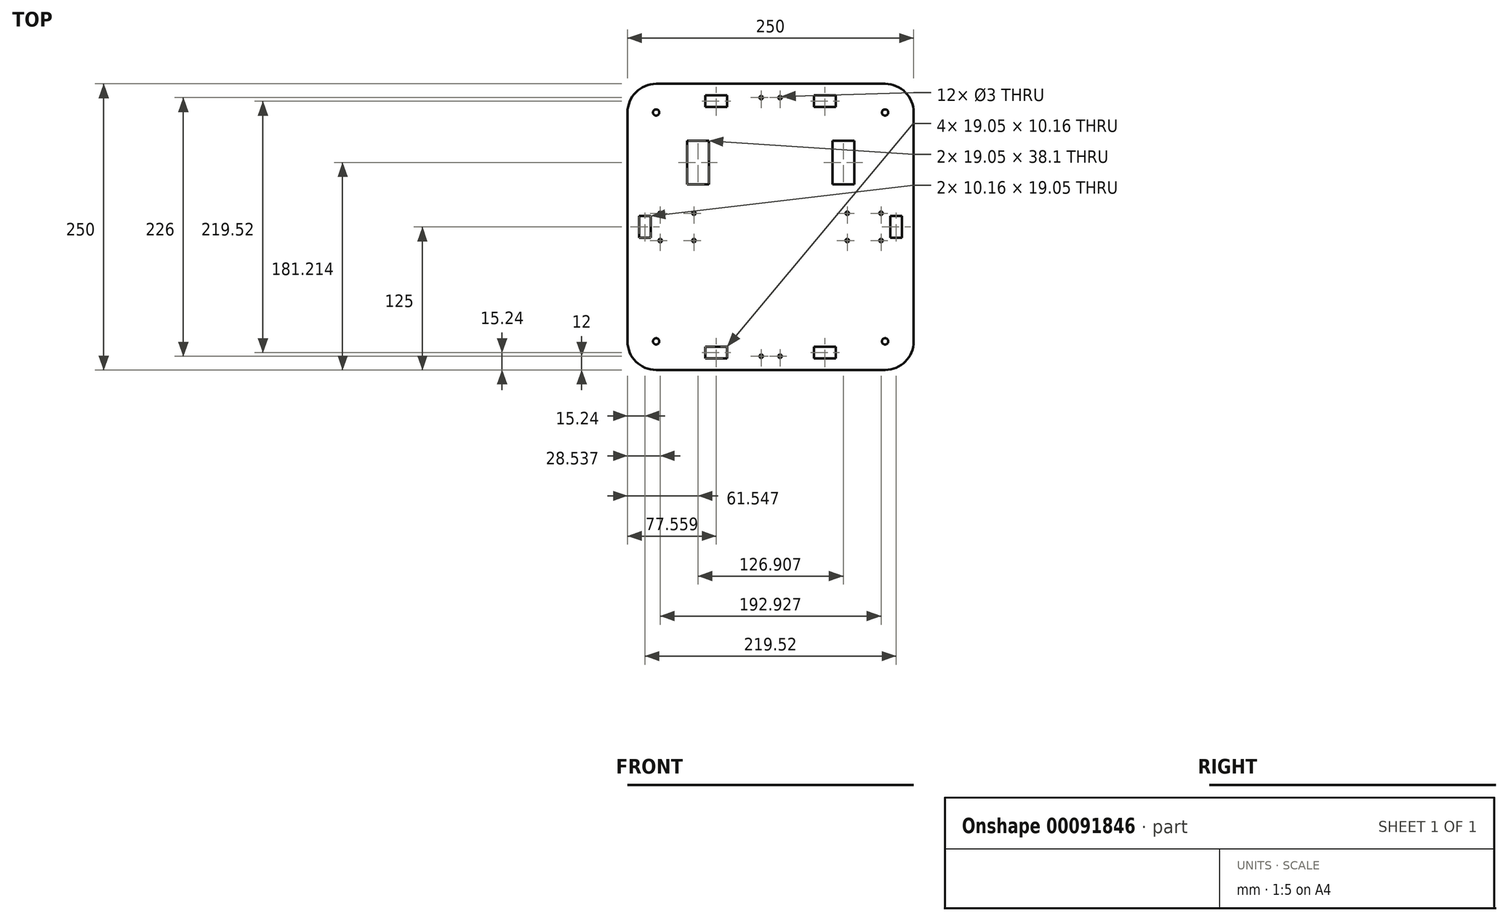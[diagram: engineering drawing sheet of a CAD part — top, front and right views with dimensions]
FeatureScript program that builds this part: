
annotation { "Feature Type Name" : "Feature", "Feature Type Description" : "" }
export const myFeature = defineFeature(function(context is Context, id is Id, definition is map)
    precondition{}
    {
        {
            var Q0;
            Q0=qCreatedBy(makeId("Top.planeOp"),FACE);
            var sketch = newSketch(context, id + "F0", { "sketchPlane" : qUnion([Q0])});
            skLineSegment(sketch, "E0.bottom", {"start": v(-100, 125) * mm, "end": v(100, 125) * mm});
            skLineSegment(sketch, "E0.top", {"start": v(-100, -125) * mm, "end": v(100, -125) * mm});
            skLineSegment(sketch, "E0.left", {"start": v(-125, 100) * mm, "end": v(-125, -100) * mm});
            skLineSegment(sketch, "E0.right", {"start": v(125, 100) * mm, "end": v(125, -100) * mm});
            skPoint(sketch, "E1.visualSharp", {"position": v(-125, -125) * mm});
            skArc(sketch, "E1.filletArc", {"start": v(-125, -100) * mm, "mid": v(-117.68, -117.68) * mm, "end": v(-100, -125) * mm});
            skPoint(sketch, "E2.visualSharp", {"position": v(-125, 125) * mm});
            skArc(sketch, "E2.filletArc", {"start": v(-100, 125) * mm, "mid": v(-117.68, 117.68) * mm, "end": v(-125, 100) * mm});
            skPoint(sketch, "E3.visualSharp", {"position": v(125, -125) * mm});
            skArc(sketch, "E3.filletArc", {"start": v(100, -125) * mm, "mid": v(117.68, -117.68) * mm, "end": v(125, -100) * mm});
            skPoint(sketch, "E4.visualSharp", {"position": v(125, 125) * mm});
            skArc(sketch, "E4.filletArc", {"start": v(125, 100) * mm, "mid": v(117.68, 117.68) * mm, "end": v(100, 125) * mm});
            skPoint(sketch, "E5", {"position": v(0, -125) * mm});
            skPoint(sketch, "E6", {"position": v(-8.23, -113) * mm});
            skCircle(sketch, "E7", {"center": v(-8.23, -113) * mm, "radius": 1.5 * mm});
            skLineSegment(sketch, "E8.bottom", {"start": v(-56.97, 104.68) * mm, "end": v(-37.92, 104.68) * mm});
            skLineSegment(sketch, "E8.top", {"start": v(-56.97, 114.84) * mm, "end": v(-37.92, 114.84) * mm});
            skLineSegment(sketch, "E8.left", {"start": v(-56.97, 104.68) * mm, "end": v(-56.97, 114.84) * mm});
            skLineSegment(sketch, "E8.right", {"start": v(-37.92, 104.68) * mm, "end": v(-37.92, 114.84) * mm});
            skPoint(sketch, "E8.middle", {"position": v(-47.44, 109.76) * mm});
            skLineSegment(sketch, "E9.MirrorCS", {"start": v(56.97, 114.84) * mm, "end": v(37.92, 114.84) * mm});
            skLineSegment(sketch, "E10.MirrorCS", {"start": v(56.97, 104.68) * mm, "end": v(56.97, 114.84) * mm});
            skLineSegment(sketch, "E11.MirrorCS", {"start": v(56.97, 104.68) * mm, "end": v(37.92, 104.68) * mm});
            skLineSegment(sketch, "E12.MirrorCS", {"start": v(37.92, 104.68) * mm, "end": v(37.92, 114.84) * mm});
            skPoint(sketch, "E13.MirrorP", {"position": v(47.44, 109.76) * mm});
            skLineSegment(sketch, "E14", {"start": v(-125, 0) * mm, "end": v(125, 0) * mm, "construction": true});
            skLineSegment(sketch, "E15.MirrorCS", {"start": v(-56.97, -104.68) * mm, "end": v(-37.92, -104.68) * mm});
            skLineSegment(sketch, "E16.MirrorCS", {"start": v(-37.92, -104.68) * mm, "end": v(-37.92, -114.84) * mm});
            skLineSegment(sketch, "E17.MirrorCS", {"start": v(-56.97, -114.84) * mm, "end": v(-37.92, -114.84) * mm});
            skLineSegment(sketch, "E18.MirrorCS", {"start": v(-56.97, -104.68) * mm, "end": v(-56.97, -114.84) * mm});
            skLineSegment(sketch, "E19.MirrorCS", {"start": v(37.92, -104.68) * mm, "end": v(37.92, -114.84) * mm});
            skLineSegment(sketch, "E20.MirrorCS", {"start": v(56.97, -114.84) * mm, "end": v(37.92, -114.84) * mm});
            skLineSegment(sketch, "E21.MirrorCS", {"start": v(56.97, -104.68) * mm, "end": v(56.97, -114.84) * mm});
            skLineSegment(sketch, "E22.MirrorCS", {"start": v(56.97, -104.68) * mm, "end": v(37.92, -104.68) * mm});
            skLineSegment(sketch, "E23", {"start": v(47.44, 109.76) * mm, "end": v(47.44, 125) * mm, "construction": true});
            skLineSegment(sketch, "E24", {"start": v(125, -17.42) * mm, "end": v(109.76, -17.42) * mm, "construction": true});
            skLineSegment(sketch, "E25.bottom", {"start": v(104.68, 9.53) * mm, "end": v(114.84, 9.53) * mm});
            skLineSegment(sketch, "E25.top", {"start": v(104.68, -9.53) * mm, "end": v(114.84, -9.53) * mm});
            skLineSegment(sketch, "E25.left", {"start": v(104.68, 9.53) * mm, "end": v(104.68, -9.53) * mm});
            skLineSegment(sketch, "E25.right", {"start": v(114.84, 9.53) * mm, "end": v(114.84, -9.53) * mm});
            skPoint(sketch, "E25.middle", {"position": v(109.76, 0) * mm});
            skLineSegment(sketch, "E26", {"start": v(0, 125) * mm, "end": v(0, -125) * mm, "construction": true});
            skLineSegment(sketch, "E27.MirrorCS", {"start": v(-104.68, 9.52) * mm, "end": v(-114.84, 9.52) * mm});
            skLineSegment(sketch, "E28.MirrorCS", {"start": v(-104.68, 9.53) * mm, "end": v(-104.68, -9.52) * mm});
            skLineSegment(sketch, "E29.MirrorCS", {"start": v(-104.68, -9.53) * mm, "end": v(-114.84, -9.53) * mm});
            skLineSegment(sketch, "E30.MirrorCS", {"start": v(-114.84, 9.53) * mm, "end": v(-114.84, -9.52) * mm});
            skPoint(sketch, "E31.MirrorP", {"position": v(-109.76, 0) * mm});
            skCircle(sketch, "E32", {"center": v(-100, 100) * mm, "radius": 2.76 * mm});
            skCircle(sketch, "E33.MirrorC", {"center": v(100, 100) * mm, "radius": 2.76 * mm});
            skCircle(sketch, "E34.MirrorC", {"center": v(100, -100) * mm, "radius": 2.76 * mm});
            skCircle(sketch, "E35.MirrorC", {"center": v(-100, -100) * mm, "radius": 2.76 * mm});
            skLineSegment(sketch, "E36.bottom", {"start": v(-43.18, 84.15) * mm, "end": v(43.18, 84.15) * mm, "construction": true});
            skLineSegment(sketch, "E36.top", {"start": v(-43.18, 28.27) * mm, "end": v(43.18, 28.27) * mm, "construction": true});
            skLineSegment(sketch, "E36.left", {"start": v(-43.18, 84.15) * mm, "end": v(-43.18, 28.27) * mm, "construction": true});
            skLineSegment(sketch, "E36.right", {"start": v(43.18, 84.15) * mm, "end": v(43.18, 28.27) * mm, "construction": true});
            skPoint(sketch, "E36.middle", {"position": v(0, 56.21) * mm});
            skLineSegment(sketch, "E37.bottom", {"start": v(-51, -86.64) * mm, "end": v(51, -86.64) * mm, "construction": true});
            skLineSegment(sketch, "E37.top", {"start": v(-51, -33.81) * mm, "end": v(51, -33.81) * mm, "construction": true});
            skLineSegment(sketch, "E37.left", {"start": v(-51, -86.64) * mm, "end": v(-51, -33.81) * mm, "construction": true});
            skLineSegment(sketch, "E37.right", {"start": v(51, -86.64) * mm, "end": v(51, -33.81) * mm, "construction": true});
            skPoint(sketch, "E37.middle", {"position": v(0, -60.23) * mm});
            skLineSegment(sketch, "E38", {"start": v(0, 56.21) * mm, "end": v(0, -60.23) * mm, "construction": true});
            skLineSegment(sketch, "E39.bottom", {"start": v(-72.98, 75.26) * mm, "end": v(-53.93, 75.26) * mm});
            skLineSegment(sketch, "E39.top", {"start": v(-72.98, 37.16) * mm, "end": v(-53.93, 37.16) * mm});
            skLineSegment(sketch, "E39.left", {"start": v(-72.98, 75.26) * mm, "end": v(-72.98, 37.16) * mm});
            skLineSegment(sketch, "E39.right", {"start": v(-53.93, 75.26) * mm, "end": v(-53.93, 37.16) * mm});
            skPoint(sketch, "E39.middle", {"position": v(-63.45, 56.21) * mm});
            skPoint(sketch, "E39.middle.positionSnap0", {"position": v(-43.18, 56.21) * mm});
            skPoint(sketch, "E39.centerSnap0", {"position": v(-43.18, 56.21) * mm});
            skLineSegment(sketch, "E40.MirrorCS", {"start": v(53.93, 75.26) * mm, "end": v(53.93, 37.16) * mm});
            skLineSegment(sketch, "E41.MirrorCS", {"start": v(72.98, 75.26) * mm, "end": v(53.93, 75.26) * mm});
            skLineSegment(sketch, "E42.MirrorCS", {"start": v(72.98, 75.26) * mm, "end": v(72.98, 37.16) * mm});
            skLineSegment(sketch, "E43.MirrorCS", {"start": v(72.98, 37.16) * mm, "end": v(53.93, 37.16) * mm});
            skLineSegment(sketch, "E44.bottom", {"start": v(-28.18, 22.65) * mm, "end": v(29.22, 22.65) * mm, "construction": true});
            skLineSegment(sketch, "E44.top", {"start": v(-28.18, -27.65) * mm, "end": v(29.22, -27.65) * mm, "construction": true});
            skLineSegment(sketch, "E44.left", {"start": v(-28.18, 22.65) * mm, "end": v(-28.18, -27.65) * mm, "construction": true});
            skLineSegment(sketch, "E44.right", {"start": v(29.22, 22.65) * mm, "end": v(29.22, -27.65) * mm, "construction": true});
            skLineSegment(sketch, "E45.bottom", {"start": v(66.96, 11.94) * mm, "end": v(96.46, 11.94) * mm, "construction": true});
            skLineSegment(sketch, "E45.top", {"start": v(66.96, -11.93) * mm, "end": v(96.46, -11.93) * mm, "construction": true});
            skLineSegment(sketch, "E45.left", {"start": v(66.96, 11.94) * mm, "end": v(66.96, -11.93) * mm, "construction": true});
            skLineSegment(sketch, "E45.right", {"start": v(96.46, 11.94) * mm, "end": v(96.46, -11.93) * mm, "construction": true});
            skPoint(sketch, "E45.middle", {"position": v(81.71, 0) * mm});
            skLineSegment(sketch, "E46", {"start": v(81.71, 11.94) * mm, "end": v(81.71, -11.93) * mm, "construction": true});
            skCircle(sketch, "E47", {"center": v(66.96, 11.94) * mm, "radius": 1.5 * mm});
            skCircle(sketch, "E48.MirrorC", {"center": v(96.46, 11.94) * mm, "radius": 1.5 * mm});
            skCircle(sketch, "E49.MirrorC", {"center": v(96.46, -11.94) * mm, "radius": 1.5 * mm});
            skCircle(sketch, "E50.MirrorC", {"center": v(66.96, -11.94) * mm, "radius": 1.5 * mm});
            skCircle(sketch, "E51.MirrorC", {"center": v(-96.46, -11.93) * mm, "radius": 1.5 * mm});
            skCircle(sketch, "E52.MirrorC", {"center": v(-96.46, 11.94) * mm, "radius": 1.5 * mm});
            skCircle(sketch, "E53.MirrorC", {"center": v(-66.96, 11.94) * mm, "radius": 1.5 * mm});
            skCircle(sketch, "E54.MirrorC", {"center": v(-66.96, -11.94) * mm, "radius": 1.5 * mm});
            skCircle(sketch, "E55.MirrorC", {"center": v(8.23, -113) * mm, "radius": 1.5 * mm});
            skCircle(sketch, "E56.MirrorC", {"center": v(-8.23, 113) * mm, "radius": 1.5 * mm});
            skCircle(sketch, "E57.MirrorC", {"center": v(8.23, 113) * mm, "radius": 1.5 * mm});
            skSolve(sketch);
        }
        {
            var Q0;
            Q0=makeQuery(id+"F0.imprint","IMPRINT",FACE,{"disambiguationData":[TD([[makeQuery(id+"F0.imprint","IMPRINT",EDGE,{"derivedFrom":sQuery(id+"F0.wireOp",EDGE,"E0.bottom")}),-1.0]])]});
            extrude(context, id + "F1", {"entities" : qUnion([Q0]), "depth" : 1 / 203.2 * mm});
        }
    });
